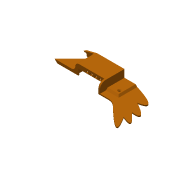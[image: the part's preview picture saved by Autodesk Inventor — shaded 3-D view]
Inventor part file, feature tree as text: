
AUTODESK INVENTOR PART (.ipt)
format: ipt  version: 2016 (Build 200138000, 138)  size: 189,952 bytes
history: native  units: in
note: dims shown in document units (in); Inventor stores cm internally (conversion verified against a paired STEP export)
features: other x3, sketch x1
ambient origin geometry x8: Origin, YZ Plane, XZ Plane, XY Plane, X Axis, Y Axis, Z Axis, Center Point
bodies: Solid1 (feature_tree)
feature tree (4):
  other  "P_akle02back_001.ipt"
  other  "Solid1::P_akle02back_001.ipt"
  other  "TaggingFeature1"
  sketch  "Sketch1"  dims[d0=0.3937in]
